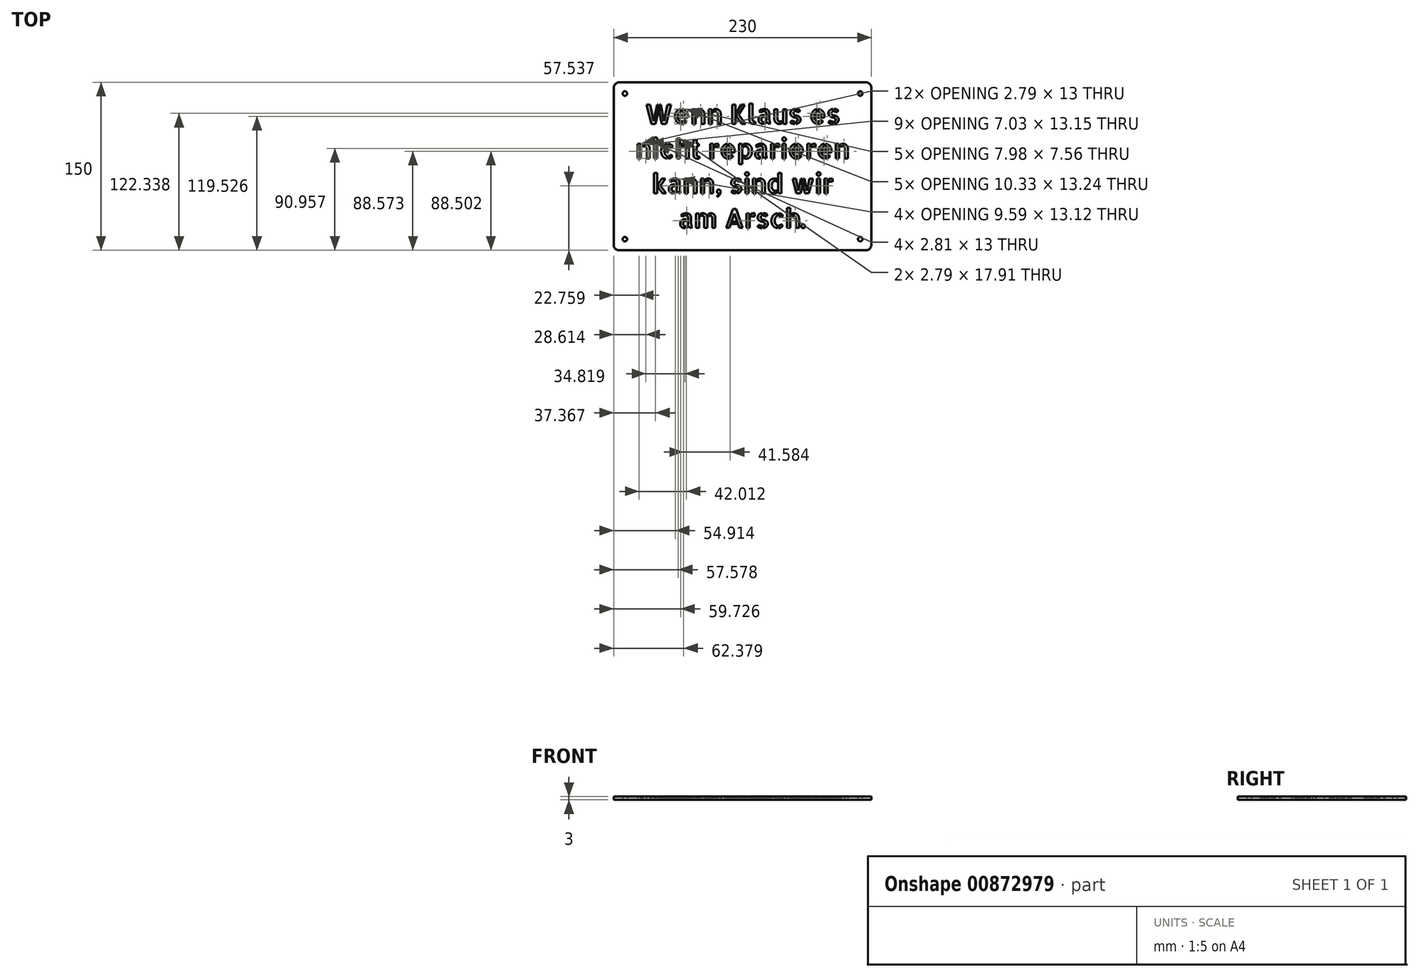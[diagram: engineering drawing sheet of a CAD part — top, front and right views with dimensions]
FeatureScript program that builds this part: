
annotation { "Feature Type Name" : "Feature", "Feature Type Description" : "" }
export const myFeature = defineFeature(function(context is Context, id is Id, definition is map)
    precondition{}
    {
        {
            var Q0;
            Q0=qCreatedBy(makeId("Top.planeOp"),FACE);
            var sketch = newSketch(context, id + "F0", { "sketchPlane" : qUnion([Q0])});
            skLineSegment(sketch, "E0.bottom", {"start": v(-98.43, 75.41) * mm, "end": v(121.57, 75.41) * mm});
            skLineSegment(sketch, "E0.top", {"start": v(-98.43, -74.59) * mm, "end": v(121.57, -74.59) * mm});
            skLineSegment(sketch, "E0.left", {"start": v(-103.43, 70.41) * mm, "end": v(-103.43, -69.59) * mm});
            skLineSegment(sketch, "E0.right", {"start": v(126.57, 70.41) * mm, "end": v(126.57, -69.59) * mm});
            skPoint(sketch, "E1.visualSharp", {"position": v(-103.43, 75.41) * mm});
            skArc(sketch, "E1.filletArc", {"start": v(-98.43, 75.41) * mm, "mid": v(-101.97, 73.95) * mm, "end": v(-103.43, 70.41) * mm});
            skPoint(sketch, "E2.visualSharp", {"position": v(126.57, 75.41) * mm});
            skArc(sketch, "E2.filletArc", {"start": v(126.57, 70.41) * mm, "mid": v(125.1, 73.95) * mm, "end": v(121.57, 75.41) * mm});
            skPoint(sketch, "E3.visualSharp", {"position": v(126.57, -74.59) * mm});
            skArc(sketch, "E3.filletArc", {"start": v(121.57, -74.59) * mm, "mid": v(125.1, -73.12) * mm, "end": v(126.57, -69.59) * mm});
            skPoint(sketch, "E4.visualSharp", {"position": v(-103.43, -74.59) * mm});
            skArc(sketch, "E4.filletArc", {"start": v(-103.43, -69.59) * mm, "mid": v(-101.97, -73.12) * mm, "end": v(-98.43, -74.59) * mm});
            skText(sketch, "E5", { "text": "Wenn Klaus es", "fontName": "AllertaStencil-Regular.ttf"});
            skText(sketch, "E6", { "text": "nicht reparieren", "fontName": "AllertaStencil-Regular.ttf"});
            skText(sketch, "E7", { "text": "kann, sind wir", "fontName": "AllertaStencil-Regular.ttf"});
            skText(sketch, "E8", { "text": "am Arsch.", "fontName": "AllertaStencil-Regular.ttf"});
            skCircle(sketch, "E9", {"center": v(116.57, 65.41) * mm, "radius": 2 * mm});
            skCircle(sketch, "E10", {"center": v(116.57, -64.59) * mm, "radius": 2 * mm});
            skCircle(sketch, "E11", {"center": v(-93.43, 65.41) * mm, "radius": 2 * mm});
            skCircle(sketch, "E12", {"center": v(-93.43, -64.59) * mm, "radius": 2 * mm});
            const initialGuessF0  = {"E5": [-0.07573, 0.03841, 1, 0, 0.017], "E6": [-0.08405, 0.00741, 1, 0, 0.017], "E7": [-0.06943, -0.02359, 1, 0, 0.017], "E8": [-0.04573, -0.05459, 1, 0, 0.017]};
            skSetInitialGuess(sketch, initialGuessF0);
            skSolve(sketch);
        }
        {
            var Q0;
            Q0=makeQuery(id+"F0.imprint","IMPRINT",FACE,{"disambiguationData":[TD([[makeQuery(id+"F0.imprint","IMPRINT",EDGE,{"derivedFrom":sQuery(id+"F0.wireOp",EDGE,"E0.bottom")}),-1.0]])]});
            extrude(context, id + "F1", {"entities" : qUnion([Q0]), "depth" : 3 * mm, "offsetDistance" : 25 * mm});
        }
    });
